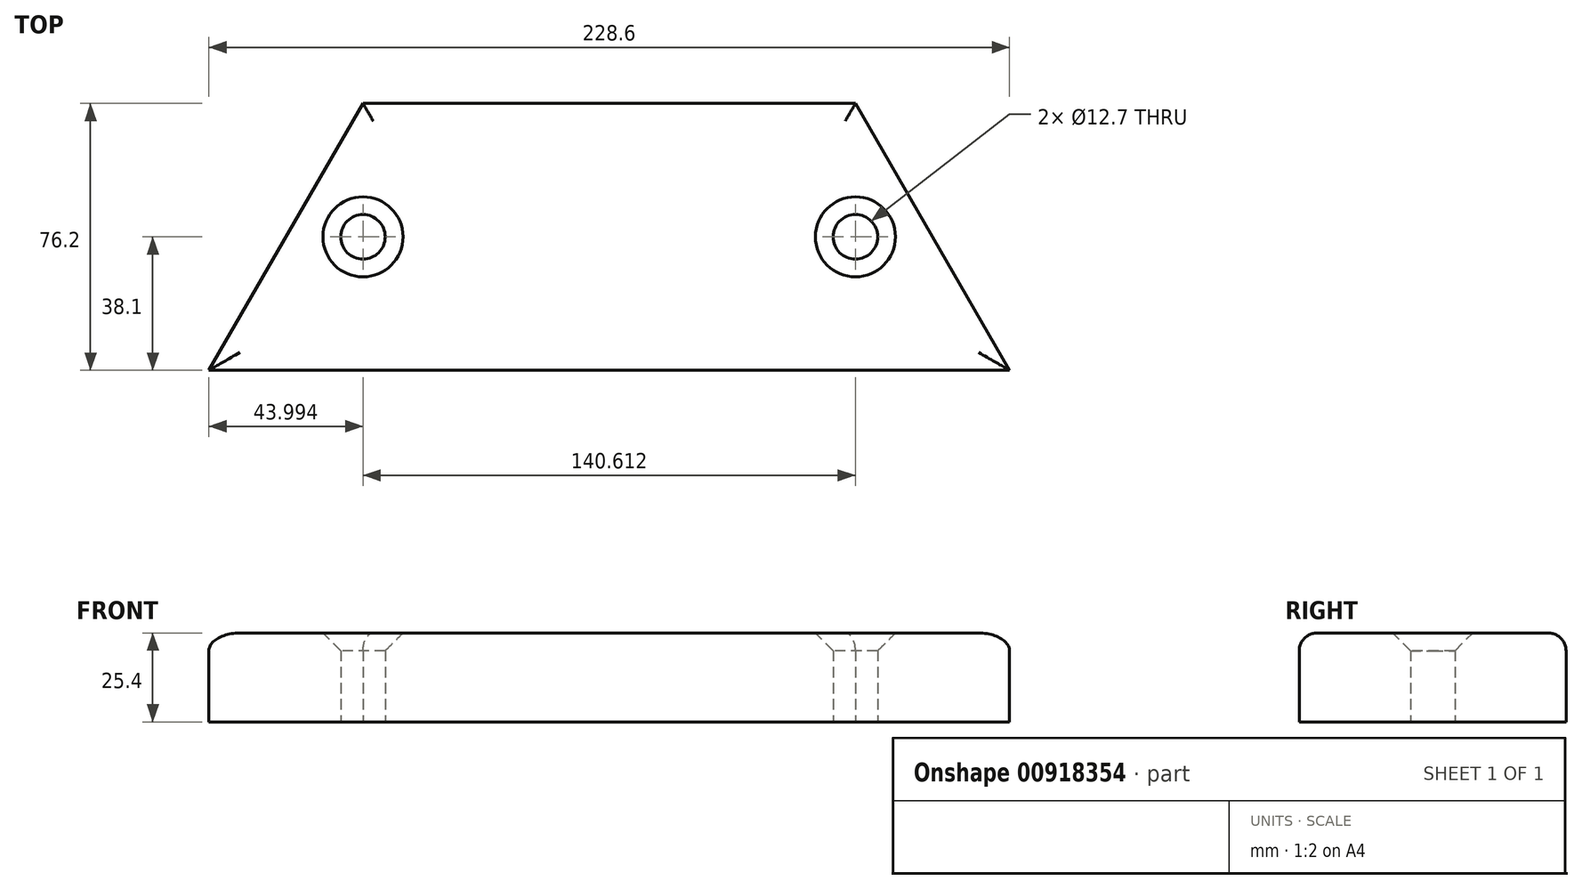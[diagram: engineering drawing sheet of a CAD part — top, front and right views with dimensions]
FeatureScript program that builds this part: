
annotation { "Feature Type Name" : "Feature", "Feature Type Description" : "" }
export const myFeature = defineFeature(function(context is Context, id is Id, definition is map)
    precondition{}
    {
        {
            var Q0;
            Q0=qCreatedBy(makeId("Top.planeOp"),FACE);
            var sketch = newSketch(context, id + "F0", { "sketchPlane" : qUnion([Q0])});
            skLineSegment(sketch, "E0.bottom", {"start": v(70.3, 38.1) * mm, "end": v(-70.3, 38.1) * mm});
            skLineSegment(sketch, "E0.top", {"start": v(70.3, -38.1) * mm, "end": v(-70.3, -38.1) * mm});
            skLineSegment(sketch, "E0.left", {"start": v(70.3, 38.1) * mm, "end": v(70.3, -38.1) * mm});
            skLineSegment(sketch, "E0.right", {"start": v(-70.3, 38.1) * mm, "end": v(-70.3, -38.1) * mm});
            skPoint(sketch, "E0.middle", {"position": v(0, 0) * mm});
            skLineSegment(sketch, "E1", {"start": v(-70.3, 38.1) * mm, "end": v(-114.3, -38.1) * mm});
            skLineSegment(sketch, "E2", {"start": v(-114.3, -38.1) * mm, "end": v(-70.3, -38.1) * mm});
            skLineSegment(sketch, "E3", {"start": v(70.3, -38.1) * mm, "end": v(114.3, -38.1) * mm});
            skLineSegment(sketch, "E4", {"start": v(114.3, -38.1) * mm, "end": v(70.3, 38.1) * mm});
            skCircle(sketch, "E5", {"center": v(-70.3, 0) * mm, "radius": 6.35 * mm});
            skCircle(sketch, "E6", {"center": v(70.3, 0) * mm, "radius": 6.35 * mm});
            skSolve(sketch);
        }
        {
            var Q0;
            {var subQ1=sQuery(id+"F0.wireOp",EDGE,"E1");Q0=makeQuery(id+"F0.imprint","IMPRINT",FACE,{"disambiguationData":[TD([[makeQuery(id+"F0.imprint","IMPRINT",EDGE,{"derivedFrom":subQ1}),1.0]])]});}
            var Q1;
            {var subQ4=sQuery(id+"F0.wireOp",EDGE,"E0.bottom");Q1=makeQuery(id+"F0.imprint","IMPRINT",FACE,{"disambiguationData":[TD([[makeQuery(id+"F0.imprint","IMPRINT",EDGE,{"derivedFrom":subQ4}),1.0]])]});}
            var Q2;
            {var subQ1=sQuery(id+"F0.wireOp",EDGE,"E3");Q2=makeQuery(id+"F0.imprint","IMPRINT",FACE,{"disambiguationData":[TD([[makeQuery(id+"F0.imprint","IMPRINT",EDGE,{"derivedFrom":subQ1}),1.0]])]});}
            extrude(context, id + "F1", {"entities" : qUnion([Q0, Q1, Q2]), "depth" : 25.4 * mm, "offsetDistance" : 25.4 * mm});
        }
        {
            var Q0;
            Q0=makeQuery(id+"F1.opExtrude","CAP_EDGE",EDGE,{"disambiguationData":[OSD([sQuery(id+"F0.wireOp",EDGE,"E5")])],"isStart":false});
            var Q1;
            Q1=makeQuery(id+"F1.opExtrude","CAP_EDGE",EDGE,{"disambiguationData":[OSD([sQuery(id+"F0.wireOp",EDGE,"E6")])],"isStart":false});
            chamfer(context, id + "F2", {"entities" : qUnion([Q0, Q1]), "width" : 5.08 * mm, "tangentPropagation" : true});
        }
        {
            var Q0;
            Q0=makeQuery(id+"F1.opExtrude","CAP_EDGE",EDGE,{"disambiguationData":[OSD([sQuery(id+"F0.wireOp",EDGE,"E0.top"),sQuery(id+"F0.wireOp",EDGE,"E2"),sQuery(id+"F0.wireOp",EDGE,"E3")])],"isStart":false});
            var Q1;
            Q1=makeQuery(id+"F1.opExtrude","CAP_EDGE",EDGE,{"disambiguationData":[OSD([sQuery(id+"F0.wireOp",EDGE,"E1")])],"isStart":false});
            var Q2;
            Q2=makeQuery(id+"F1.opExtrude","CAP_EDGE",EDGE,{"disambiguationData":[OSD([sQuery(id+"F0.wireOp",EDGE,"E0.bottom")])],"isStart":false});
            var Q3;
            Q3=makeQuery(id+"F1.opExtrude","CAP_EDGE",EDGE,{"disambiguationData":[OSD([sQuery(id+"F0.wireOp",EDGE,"E4")])],"isStart":false});
            fillet(context, id + "F3", {"entities" : qUnion([Q0, Q1, Q2, Q3]), "radius" : 5.08 * mm, "tangentPropagation" : true, "allowEdgeOverflow" : false});
        }
    });
